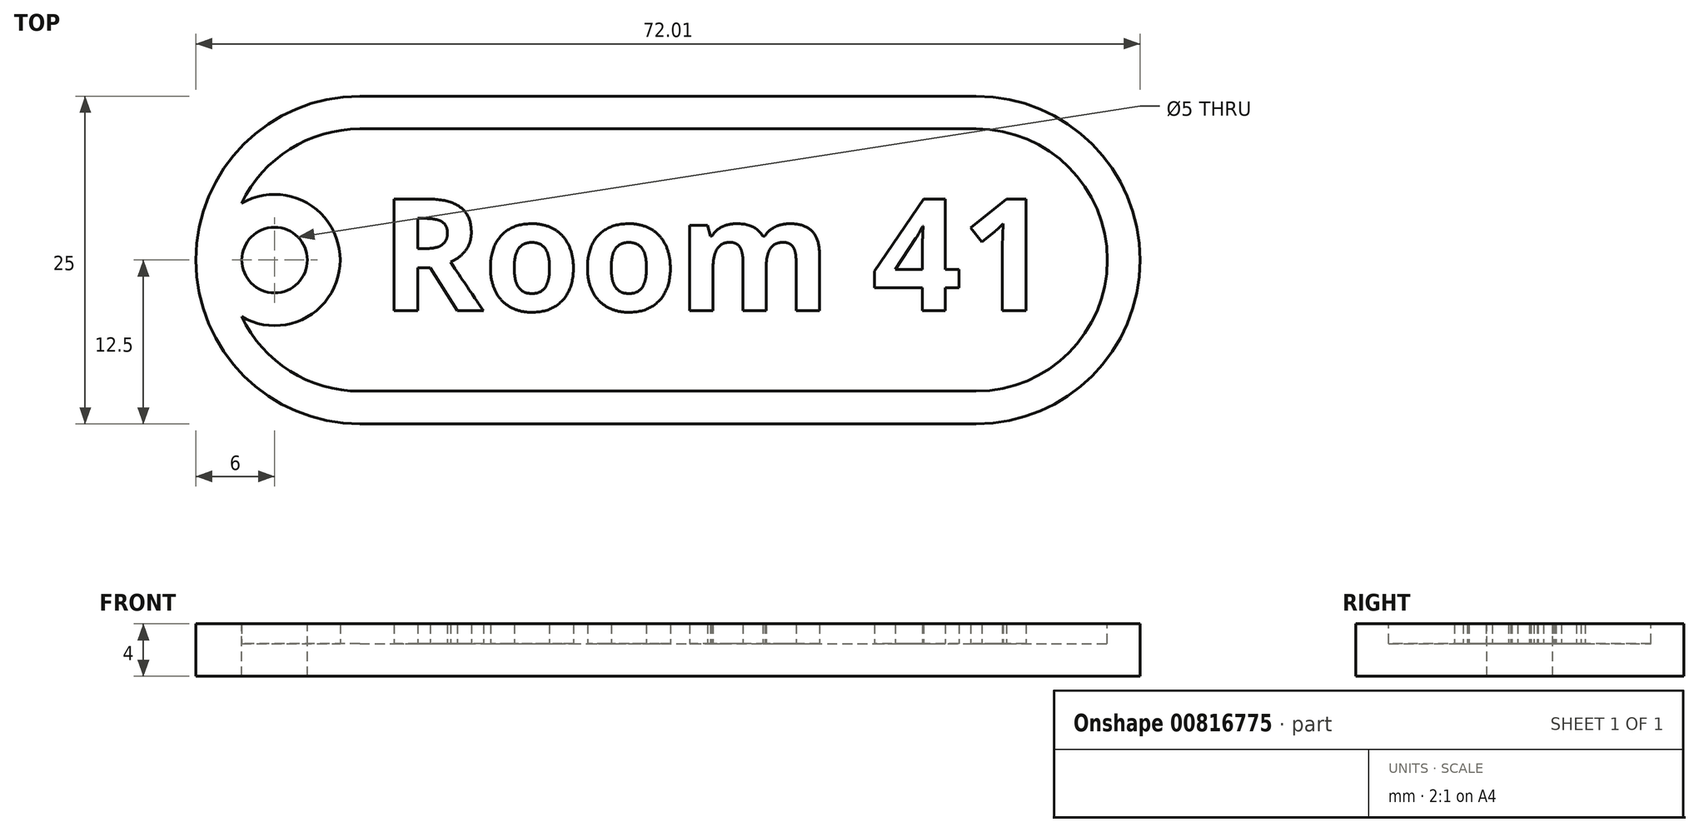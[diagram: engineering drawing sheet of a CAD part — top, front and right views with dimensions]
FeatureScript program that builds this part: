
annotation { "Feature Type Name" : "Feature", "Feature Type Description" : "" }
export const myFeature = defineFeature(function(context is Context, id is Id, definition is map)
    precondition{}
    {
        {
            var Q0;
            Q0=qCreatedBy(makeId("Top.planeOp"),FACE);
            var sketch = newSketch(context, id + "F0", { "sketchPlane" : qUnion([Q0])});
            skLineSegment(sketch, "E0.bottom", {"start": v(12.5, 0) * mm, "end": v(59.5, 0) * mm});
            skLineSegment(sketch, "E0.top", {"start": v(12.5, 25) * mm, "end": v(59.5, 25) * mm});
            skArc(sketch, "E1", {"start": v(12.5, 25) * mm, "mid": v(0, 12.5) * mm, "end": v(12.5, 0) * mm});
            skPoint(sketch, "E1.centerSnap0", {"position": v(0, 12.5) * mm});
            skArc(sketch, "E2", {"start": v(59.5, 0) * mm, "mid": v(72, 12.5) * mm, "end": v(59.5, 25) * mm});
            skPoint(sketch, "E2.centerSnap0", {"position": v(75, 12.5) * mm});
            skPoint(sketch, "E3.orphan", {"position": v(0, 25) * mm});
            skPoint(sketch, "E0.left.start.orphan", {"position": v(0, 0) * mm});
            skPoint(sketch, "E4.orphan", {"position": v(75, 25) * mm});
            skPoint(sketch, "E5.orphan", {"position": v(75, 0) * mm});
            skSolve(sketch);
        }
        {
            var Q0;
            Q0=makeQuery(id+"F0.imprint","IMPRINT",FACE,{"disambiguationData":[TD([[makeQuery(id+"F0.imprint","IMPRINT",EDGE,{"derivedFrom":sQuery(id+"F0.wireOp",EDGE,"E0.bottom")}),1.0]])]});
            extrude(context, id + "F1", {"entities" : qUnion([Q0]), "depth" : 4 * mm, "offsetDistance" : 25 * mm});
        }
        {
            var Q0;
            Q0=makeQuery(id+"F1.opExtrude","CAP_FACE",FACE,{"disambiguationData":[OSD([sQuery(id+"F0.wireOp",EDGE,"E0.bottom"),sQuery(id+"F0.wireOp",EDGE,"E0.top"),sQuery(id+"F0.wireOp",EDGE,"E1"),sQuery(id+"F0.wireOp",EDGE,"E2")])],"isStart":false});
            var sketch = newSketch(context, id + "F2", { "sketchPlane" : qUnion([Q0])});
            skArc(sketch, "E6", {"start": v(12.5, 22.5) * mm, "mid": v(2.5, 12.5) * mm, "end": v(12.5, 2.5) * mm});
            skArc(sketch, "E7", {"start": v(59.5, 2.5) * mm, "mid": v(69.5, 12.5) * mm, "end": v(59.5, 22.5) * mm});
            skLineSegment(sketch, "E8", {"start": v(12.5, 22.5) * mm, "end": v(59.5, 22.5) * mm});
            skLineSegment(sketch, "E9", {"start": v(12.5, 2.5) * mm, "end": v(59.5, 2.5) * mm});
            skSolve(sketch);
        }
        {
            var Q0;
            Q0=makeQuery(id+"F2.imprint","IMPRINT",FACE,{"disambiguationData":[TD([[makeQuery(id+"F2.imprint","IMPRINT",EDGE,{"derivedFrom":sQuery(id+"F2.wireOp",EDGE,"E6")}),1.0]])]});
            extrude(context, id + "F3", {"entities" : qUnion([Q0]), "operationType" : NewBodyOperationType.REMOVE, "oppositeDirection" : true, "depth" : 1.5 * mm, "offsetDistance" : 25 * mm});
        }
        {
            var Q0;
            Q0=makeQuery(id+"F3.boolean.opBoolean","COPY",FACE,{"derivedFrom":makeQuery(id+"F3.opExtrude","CAP_FACE",FACE,{"disambiguationData":[OSD([sQuery(id+"F2.wireOp",EDGE,"E6"),sQuery(id+"F2.wireOp",EDGE,"E7"),sQuery(id+"F2.wireOp",EDGE,"E8"),sQuery(id+"F2.wireOp",EDGE,"E9")])],"isStart":false})});
            var sketch = newSketch(context, id + "F4", { "sketchPlane" : qUnion([Q0])});
            skCircle(sketch, "E10", {"center": v(6, 12.5) * mm, "radius": 5 * mm});
            skPoint(sketch, "E10.centerSnap0", {"position": v(2.5, 12.5) * mm});
            skSolve(sketch);
        }
        {
            var Q0;
            {var subQ0=sQuery(id+"F4.wireOp",EDGE,"E10");var subQ1=makeQuery(id+"F3.boolean.opBoolean","COPY",EDGE,{"derivedFrom":makeQuery(id+"F3.opExtrude","CAP_EDGE",EDGE,{"disambiguationData":[OSD([sQuery(id+"F2.wireOp",EDGE,"E6")])],"isStart":false})});var subQ2=makeQuery(id+"F4.imprint","INTERSECT",VERTEX,{"disambiguationData":[OD(0.0)],"derivedFrom":[subQ1,subQ0]});Q0=makeQuery(id+"F4.imprint","IMPRINT",FACE,{"disambiguationData":[TD([[makeQuery(id+"F4.imprint","IMPRINT",EDGE,{"disambiguationData":[TD([[subQ2,1.0]])],"derivedFrom":subQ0}),1.0]])]});}
            extrude(context, id + "F5", {"entities" : qUnion([Q0]), "operationType" : NewBodyOperationType.ADD, "depth" : 1.5 * mm, "offsetDistance" : 25 * mm});
        }
        {
            var Q0;
            Q0=makeQuery(id+"F5.boolean.opBoolean","MERGE",FACE,{"derivedFrom":[makeQuery(id+"F1.opExtrude","CAP_FACE",FACE,{"disambiguationData":[OSD([sQuery(id+"F0.wireOp",EDGE,"E0.bottom"),sQuery(id+"F0.wireOp",EDGE,"E0.top"),sQuery(id+"F0.wireOp",EDGE,"E1"),sQuery(id+"F0.wireOp",EDGE,"E2")])],"isStart":false}),makeQuery(id+"F5.opExtrude","CAP_FACE",FACE,{"disambiguationData":[OSD([sQuery(id+"F2.wireOp",EDGE,"E6"),sQuery(id+"F4.wireOp",EDGE,"E10")])],"isStart":false})]});
            var sketch = newSketch(context, id + "F6", { "sketchPlane" : qUnion([Q0])});
            skCircle(sketch, "E11", {"center": v(6, 12.5) * mm, "radius": 2.5 * mm});
            skSolve(sketch);
        }
        {
            var Q0;
            Q0=makeQuery(id+"F6.imprint","IMPRINT",FACE,{"disambiguationData":[TD([[makeQuery(id+"F6.imprint","IMPRINT",EDGE,{"derivedFrom":sQuery(id+"F6.wireOp",EDGE,"E11")}),1.0]])]});
            extrude(context, id + "F7", {"entities" : qUnion([Q0]), "operationType" : NewBodyOperationType.REMOVE, "oppositeDirection" : true, "depth" : 25 * mm, "offsetDistance" : 25 * mm});
        }
        {
            var Q0;
            Q0=makeQuery(id+"F3.boolean.opBoolean","COPY",FACE,{"derivedFrom":makeQuery(id+"F3.opExtrude","CAP_FACE",FACE,{"disambiguationData":[OSD([sQuery(id+"F2.wireOp",EDGE,"E6"),sQuery(id+"F2.wireOp",EDGE,"E7"),sQuery(id+"F2.wireOp",EDGE,"E8"),sQuery(id+"F2.wireOp",EDGE,"E9")])],"isStart":false})});
            var sketch = newSketch(context, id + "F8", { "sketchPlane" : qUnion([Q0])});
            skText(sketch, "E12", { "text": "Room 41", "fontName": "OpenSans-Bold.ttf"});
            const initialGuessF8  = {"E12": [0.01404, 0.00863, 1, 0, 0.0086]};
            skSetInitialGuess(sketch, initialGuessF8);
            skSolve(sketch);
        }
        {
            var Q0;
            Q0 = qSketchRegion(id + "F8", true);
            extrude(context, id + "F9", {"entities" : qUnion([Q0]), "operationType" : NewBodyOperationType.ADD, "depth" : 1.5 * mm, "offsetDistance" : 25 * mm});
        }
    });
